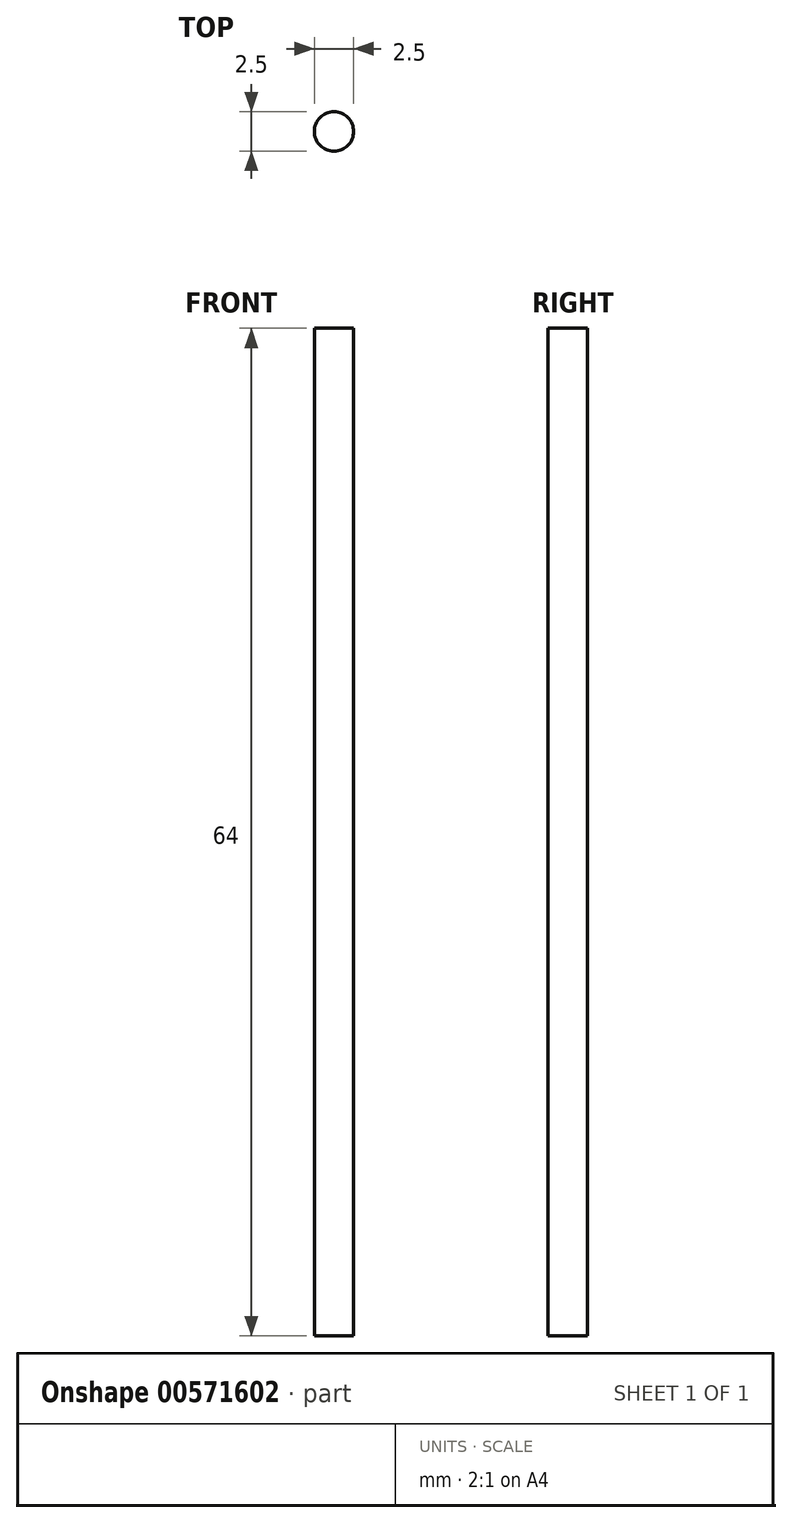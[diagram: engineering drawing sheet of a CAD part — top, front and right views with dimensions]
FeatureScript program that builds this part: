
annotation { "Feature Type Name" : "Feature", "Feature Type Description" : "" }
export const myFeature = defineFeature(function(context is Context, id is Id, definition is map)
    precondition{}
    {
        {
            var Q0;
            Q0=qCreatedBy(makeId("Top.planeOp"),FACE);
            var sketch = newSketch(context, id + "F0", { "sketchPlane" : qUnion([Q0])});
            skCircle(sketch, "E0", {"center": v(0, 0) * mm, "radius": 1.25 * mm});
            skSolve(sketch);
        }
        {
            var Q0;
            Q0 = qSketchRegion(id + "F0", true);
            extrude(context, id + "F1", {"entities" : qUnion([Q0]), "depth" : 64 * mm, "offsetDistance" : 25.4 * mm});
        }
    });
